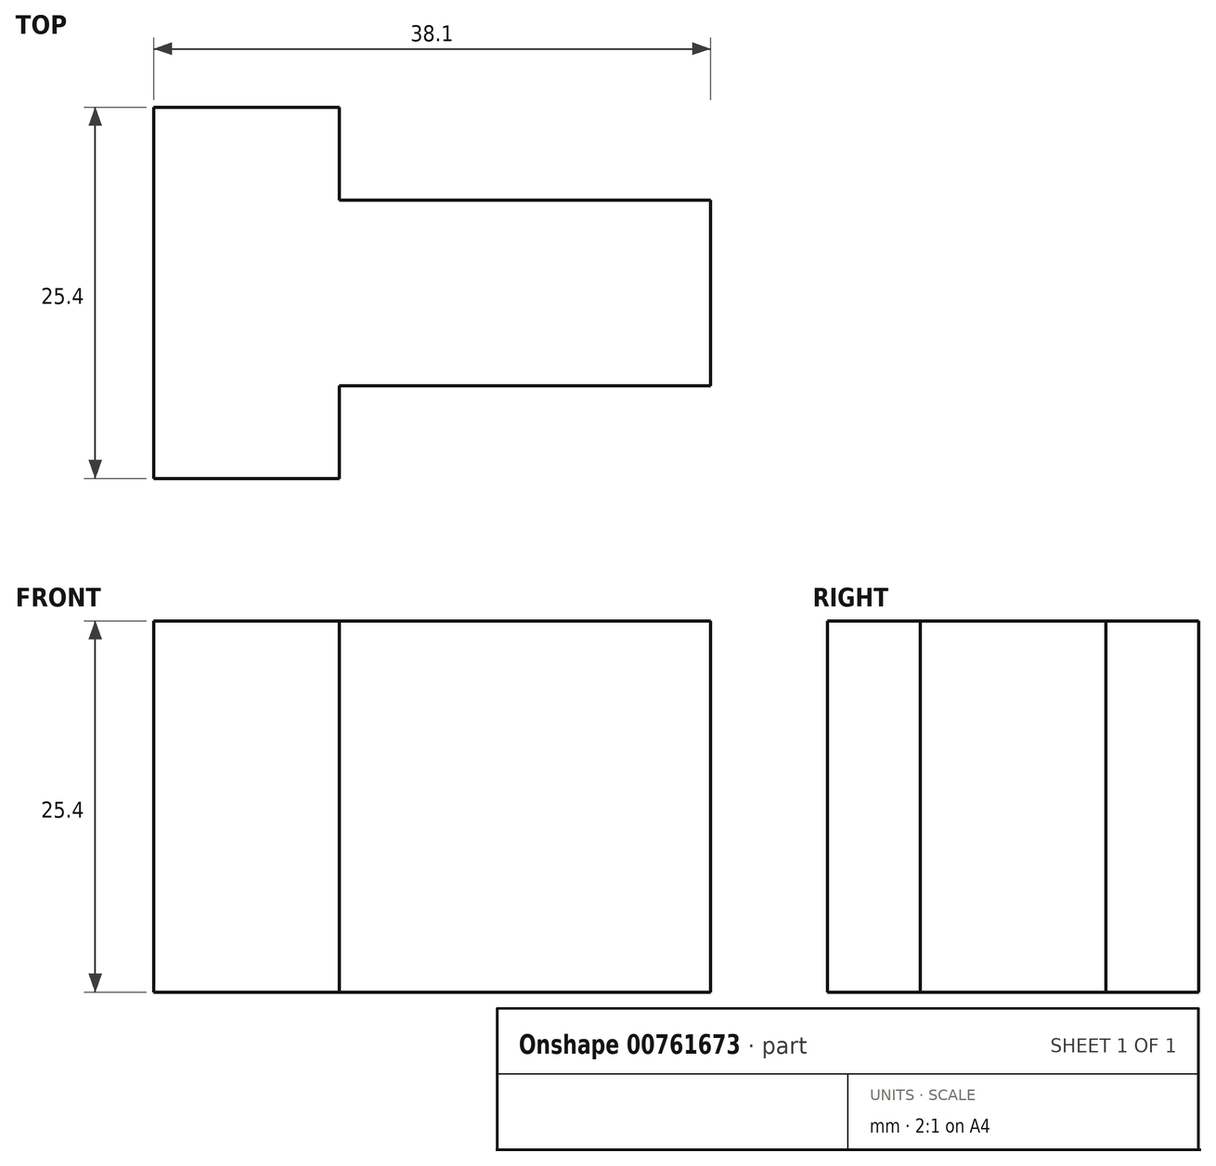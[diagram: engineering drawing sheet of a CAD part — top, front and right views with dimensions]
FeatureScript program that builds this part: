
annotation { "Feature Type Name" : "Feature", "Feature Type Description" : "" }
export const myFeature = defineFeature(function(context is Context, id is Id, definition is map)
    precondition{}
    {
        {
            var Q0;
            Q0=qCreatedBy(makeId("Top.planeOp"),FACE);
            var sketch = newSketch(context, id + "F0", { "sketchPlane" : qUnion([Q0])});
            skLineSegment(sketch, "E0", {"start": v(0, 0) * mm, "end": v(12.7, 0) * mm});
            skLineSegment(sketch, "E1", {"start": v(12.7, 0) * mm, "end": v(12.7, 6.35) * mm});
            skLineSegment(sketch, "E2", {"start": v(12.7, 6.35) * mm, "end": v(38.1, 6.35) * mm});
            skLineSegment(sketch, "E3", {"start": v(38.1, 6.35) * mm, "end": v(38.1, 19.05) * mm});
            skLineSegment(sketch, "E4", {"start": v(38.1, 19.05) * mm, "end": v(12.7, 19.05) * mm});
            skLineSegment(sketch, "E5", {"start": v(12.7, 19.05) * mm, "end": v(12.7, 25.4) * mm});
            skLineSegment(sketch, "E6", {"start": v(12.7, 25.4) * mm, "end": v(0, 25.4) * mm});
            skLineSegment(sketch, "E7", {"start": v(0, 25.4) * mm, "end": v(0, 0) * mm});
            skSolve(sketch);
        }
        {
            var Q0;
            Q0=makeQuery(id+"F0.imprint","IMPRINT",FACE,{"disambiguationData":[TD([[makeQuery(id+"F0.imprint","IMPRINT",EDGE,{"derivedFrom":sQuery(id+"F0.wireOp",EDGE,"E0")}),1.0]])]});
            var Q1;
            Q1 = qSketchRegion(id + "F0", true);
            extrude(context, id + "F1", {"entities" : qUnion([Q0, Q1]), "depth" : 25.4 * mm, "offsetDistance" : 25.4 * mm});
        }
    });
